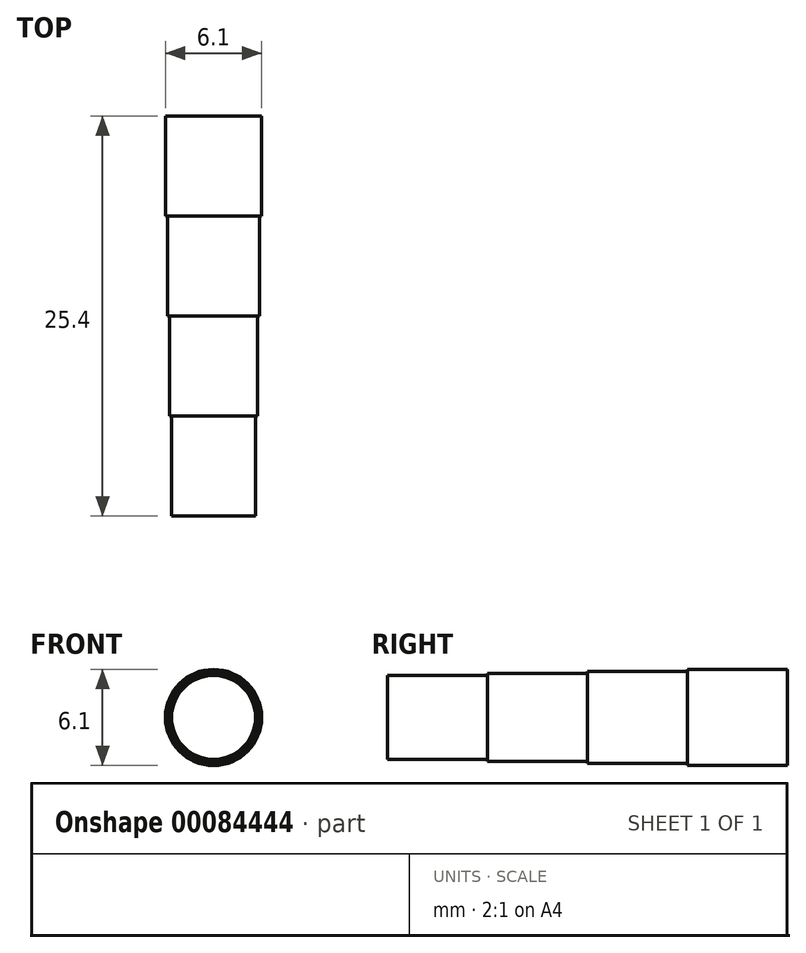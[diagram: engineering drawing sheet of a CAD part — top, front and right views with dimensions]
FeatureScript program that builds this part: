
annotation { "Feature Type Name" : "Feature", "Feature Type Description" : "" }
export const myFeature = defineFeature(function(context is Context, id is Id, definition is map)
    precondition{}
    {
        {
            var Q0;
            Q0=qCreatedBy(makeId("Front.planeOp"),FACE);
            var sketch = newSketch(context, id + "F0", { "sketchPlane" : qUnion([Q0])});
            skCircle(sketch, "E0", {"center": v(0, 0) * mm, "radius": 3.05 * mm});
            skSolve(sketch);
        }
        {
            var Q0;
            Q0=makeQuery(id+"F0.imprint","IMPRINT",FACE,{"disambiguationData":[TD([[makeQuery(id+"F0.imprint","IMPRINT",EDGE,{"derivedFrom":sQuery(id+"F0.wireOp",EDGE,"E0")}),1.0]])]});
            extrude(context, id + "F1", {"entities" : qUnion([Q0]), "depth" : 6.35 * mm});
        }
        {
            var Q0;
            Q0=makeQuery(id+"F1.opExtrude","CAP_FACE",FACE,{"disambiguationData":[OSD([sQuery(id+"F0.wireOp",EDGE,"E0")])],"isStart":false});
            var sketch = newSketch(context, id + "F2", { "sketchPlane" : qUnion([Q0])});
            skCircle(sketch, "E1", {"center": v(0, 0) * mm, "radius": 2.92 * mm});
            skSolve(sketch);
        }
        {
            var Q0;
            Q0=makeQuery(id+"F2.imprint","IMPRINT",FACE,{"disambiguationData":[TD([[makeQuery(id+"F2.imprint","IMPRINT",EDGE,{"derivedFrom":sQuery(id+"F2.wireOp",EDGE,"E1")}),1.0]])]});
            extrude(context, id + "F3", {"entities" : qUnion([Q0]), "operationType" : NewBodyOperationType.ADD, "depth" : 6.35 * mm});
        }
        {
            var Q0;
            Q0=makeQuery(id+"F3.opExtrude","CAP_FACE",FACE,{"disambiguationData":[OSD([sQuery(id+"F2.wireOp",EDGE,"E1")])],"isStart":false});
            var sketch = newSketch(context, id + "F4", { "sketchPlane" : qUnion([Q0])});
            skCircle(sketch, "E2", {"center": v(0, 0) * mm, "radius": 2.8 * mm});
            skSolve(sketch);
        }
        {
            var Q0;
            Q0=makeQuery(id+"F4.imprint","IMPRINT",FACE,{"disambiguationData":[TD([[makeQuery(id+"F4.imprint","IMPRINT",EDGE,{"derivedFrom":sQuery(id+"F4.wireOp",EDGE,"E2")}),1.0]])]});
            extrude(context, id + "F5", {"entities" : qUnion([Q0]), "operationType" : NewBodyOperationType.ADD, "depth" : 6.35 * mm});
        }
        {
            var Q0;
            Q0=makeQuery(id+"F5.opExtrude","CAP_FACE",FACE,{"disambiguationData":[OSD([sQuery(id+"F4.wireOp",EDGE,"E2")])],"isStart":false});
            var sketch = newSketch(context, id + "F6", { "sketchPlane" : qUnion([Q0])});
            skCircle(sketch, "E3", {"center": v(0, 0) * mm, "radius": 2.67 * mm});
            skSolve(sketch);
        }
        {
            var Q0;
            Q0=makeQuery(id+"F6.imprint","IMPRINT",FACE,{"disambiguationData":[TD([[makeQuery(id+"F6.imprint","IMPRINT",EDGE,{"derivedFrom":sQuery(id+"F6.wireOp",EDGE,"E3")}),1.0]])]});
            extrude(context, id + "F7", {"entities" : qUnion([Q0]), "operationType" : NewBodyOperationType.ADD, "depth" : 6.35 * mm});
        }
    });
